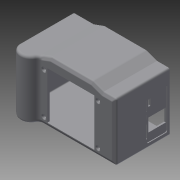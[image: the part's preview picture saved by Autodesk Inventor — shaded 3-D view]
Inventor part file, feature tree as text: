
AUTODESK INVENTOR PART (.ipt)
format: ipt  version: 2015 (Build 190159000, 159)  size: 547,328 bytes
history: native  units: in
note: dims shown in document units (in); Inventor stores cm internally (conversion verified against a paired STEP export)
features: reference x22, fillet x8, extrude x7, sketch x7, chamfer x4, projected_geometry x3, plane x1, other x1
ambient origin geometry x8: Origin, YZ Plane, XZ Plane, XY Plane, X Axis, Y Axis, Z Axis, Center Point
bodies: Body1 (feature_tree)
feature tree (53):
  plane  "Work Plane1"
  extrude  "Extrusion3"  Depth=0.1181in TaperAngle=0.0deg
  extrude  "Extrusion4"  Depth=0.9843in
  extrude  "Extrusion9"  Depth=2.3622in TaperAngle=0.0deg
  extrude  "Extrusion5"  Depth=0.1181in
  extrude  "Extrusion6"  Depth=0.0787in
  chamfer  "Chamfer1"  Distance=0.0787in
  chamfer  "Chamfer2"  Distance=0.0787in
  chamfer  "Chamfer5"  Distance=0.1969in
  fillet  "Fillet5"  Radius=0.1969in
  fillet  "Fillet6"  Radius=0.1181in
  fillet  "Fillet7"  Radius=0.1181in
  fillet  "Fillet8"  Radius=0.0787in
  fillet  "Fillet9"  Radius=0.0394in
  fillet  "Fillet10"  Radius=0.1181in
  extrude  "Extrusion7"  Depth=0.0394in
  other  "Lip1"
  extrude  "Extrusion8"  Depth=0.0394in
  chamfer  "Chamfer4"  Distance=0.1181in
  fillet  "Fillet11"  Radius=0.1575in
  fillet  "Fillet12"  Radius=0.0787in
  sketch  "Sketch3"  dims[d10=0.1181in d11=0.0in d12=0.1181in d13=2.4803in d14=0.0in]
  reference  "Reference1"
  reference  "Reference2"
  reference  "Reference3"
  reference  "Reference4"
  sketch  "Sketch4"  dims[d17=2.7724in d18=0.0in d19=0.9843in]
  projected_geometry  "Projected Loop2"
  sketch  "Sketch5"  dims[d20=0.5118in d25=2.3622in d26=0.0in]
  sketch  "Sketch6"  dims[d27=0.1181in d28=0.1181in]
  reference  "Reference16"
  reference  "Reference18"
  reference  "Reference19"
  reference  "Reference21"
  sketch  "Sketch7"  dims[d29=0.5118in d30=0.1969in d31=0.1575in d32=0.0787in d33=0.1374in d34=0.1575in d35=0.0787in d36=0.1374in]
  reference  "Reference23"
  reference  "Reference24"
  reference  "Reference25"
  reference  "Reference26"
  reference  "Reference28"
  reference  "Reference31"
  reference  "Reference32"
  reference  "Reference33"
  reference  "Reference34"
  reference  "Reference35"
  reference  "Reference36"
  reference  "Reference37"
  reference  "Reference38"
  sketch  "Sketch8"  dims[d40=0.0787in]
  reference  "Reference39"
  sketch  "Sketch9"  dims[d41=0.0787in d42=0.1969in d43=0.1969in d44=0.1181in d45=0.1181in d46=0.0787in d47=0.0394in d48=0.0in d49=0.0394in d50=0.0394in d51=0.0in d52=0.0in d53=0.0in d54=0.0in d55=0.1181in d56=0.315in d57=0.315in d58=0.1181in d59=0.1575in d60=0.0in d61=0.0472in d62=0.0787in d63=0.1374in d64=0.1181in d65=0.9843in d66=1.9685in d67=0.1969in d70=0.0787in d71=1.0994in d72=0.5118in d73=1.9685in d74=1.0994in d75=0.5118in d76=0.1181in d77=0.0787in d78=0.0787in d79=0.0787in d80=0.1575in d81=0.0in d82=0.1575in d83=0.0787in d84=0.1374in d85=0.0394in d86=0.0394in]
  projected_geometry  "Projected Loop3"
  projected_geometry  "Projected Loop4"
